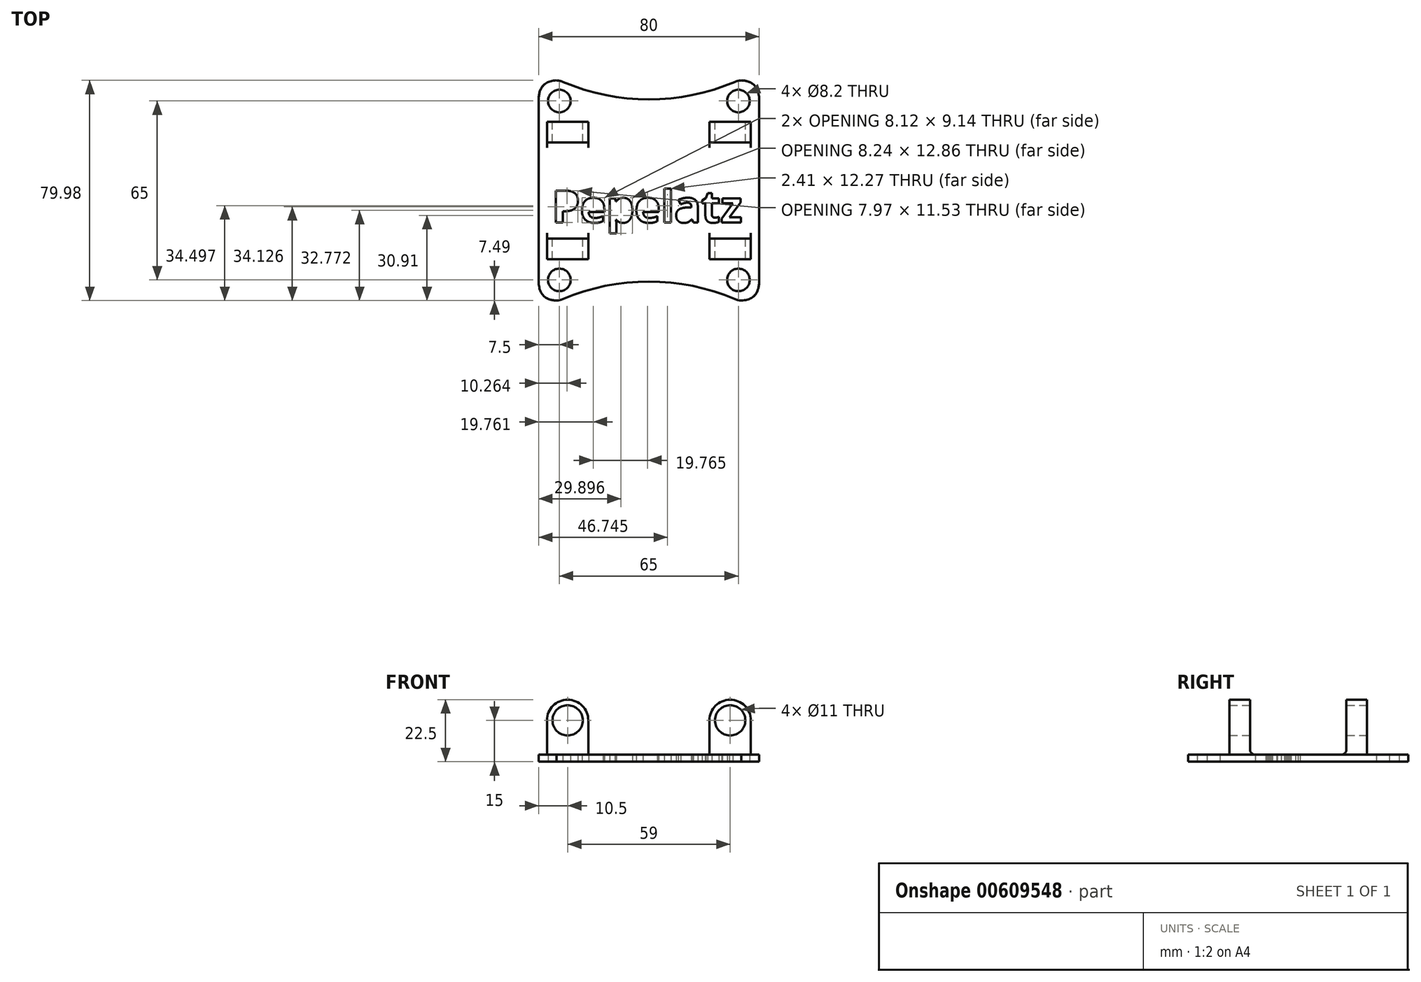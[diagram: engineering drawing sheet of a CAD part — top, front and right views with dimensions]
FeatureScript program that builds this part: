
annotation { "Feature Type Name" : "Feature", "Feature Type Description" : "" }
export const myFeature = defineFeature(function(context is Context, id is Id, definition is map)
    precondition{}
    {
        {
            var Q0;
            Q0=qCreatedBy(makeId("Top.planeOp"),FACE);
            var sketch = newSketch(context, id + "F0", { "sketchPlane" : qUnion([Q0])});
            skLineSegment(sketch, "E0.bottom", {"start": v(-40, 40) * mm, "end": v(-32.5, 40) * mm});
            skLineSegment(sketch, "E0.top", {"start": v(-40, -40) * mm, "end": v(-32.5, -40) * mm});
            skLineSegment(sketch, "E0.left", {"start": v(-40, 40) * mm, "end": v(-40, -40) * mm});
            skLineSegment(sketch, "E0.right", {"start": v(40, 40) * mm, "end": v(40, -40) * mm});
            skPoint(sketch, "E0.middle", {"position": v(0, 0) * mm});
            skLineSegment(sketch, "E1.bottom", {"start": v(-32.5, 32.5) * mm, "end": v(32.5, 32.5) * mm, "construction": true});
            skLineSegment(sketch, "E1.top", {"start": v(-32.5, -32.5) * mm, "end": v(32.5, -32.5) * mm, "construction": true});
            skLineSegment(sketch, "E1.left", {"start": v(-32.5, 32.5) * mm, "end": v(-32.5, -32.5) * mm, "construction": true});
            skLineSegment(sketch, "E1.right", {"start": v(32.5, 32.5) * mm, "end": v(32.5, -32.5) * mm, "construction": true});
            skCircle(sketch, "E2", {"center": v(-32.5, 32.5) * mm, "radius": 4.1 * mm});
            skCircle(sketch, "E3", {"center": v(32.5, 32.5) * mm, "radius": 4.1 * mm});
            skCircle(sketch, "E4", {"center": v(-32.5, -32.5) * mm, "radius": 4.1 * mm});
            skCircle(sketch, "E5", {"center": v(32.5, -32.5) * mm, "radius": 4.1 * mm});
            skLineSegment(sketch, "E6.trimOffspring", {"start": v(32.5, -40) * mm, "end": v(40, -40) * mm});
            skArc(sketch, "E7", {"start": v(32.5, -40) * mm, "mid": v(0, -33.1) * mm, "end": v(-32.5, -40) * mm});
            skPoint(sketch, "E8", {"position": v(-32.5, 40) * mm});
            skPoint(sketch, "E9", {"position": v(32.5, 40) * mm});
            skLineSegment(sketch, "E10.trimOffspring", {"start": v(32.5, 40) * mm, "end": v(40, 40) * mm});
            skArc(sketch, "E11", {"start": v(-32.5, 40) * mm, "mid": v(0, 33.1) * mm, "end": v(32.5, 40) * mm});
            skText(sketch, "E12", { "text": "Pepelatz", "fontName": "OpenSans-Bold.ttf"});
            const initialGuessF0  = {"E12": [-0.03517, -0.01163, 1, 0, 0.01163]};
            skSetInitialGuess(sketch, initialGuessF0);
            skSolve(sketch);
        }
        {
            var Q0;
            Q0 = qSketchRegion(id + "F0", true);
            extrude(context, id + "F1", {"entities" : qUnion([Q0]), "depth" : 2.5 * mm, "offsetDistance" : 25 * mm});
        }
        {
            var Q0;
            Q0=makeQuery(id+"F1.opExtrude","SWEPT_EDGE",EDGE,{"disambiguationData":[OSD([sQuery(id+"F0.wireOp",EDGE,"E0.bottom"),sQuery(id+"F0.wireOp",EDGE,"E0.right")])]});
            var Q1;
            Q1=makeQuery(id+"F1.opExtrude","SWEPT_EDGE",EDGE,{"disambiguationData":[OSD([sQuery(id+"F0.wireOp",EDGE,"E0.top"),sQuery(id+"F0.wireOp",EDGE,"E0.left")])]});
            var Q2;
            Q2=makeQuery(id+"F1.opExtrude","SWEPT_EDGE",EDGE,{"disambiguationData":[OSD([sQuery(id+"F0.wireOp",EDGE,"E0.right"),sQuery(id+"F0.wireOp",EDGE,"E6.trimOffspring")])]});
            var Q3;
            Q3=makeQuery(id+"F1.opExtrude","SWEPT_EDGE",EDGE,{"disambiguationData":[OSD([sQuery(id+"F0.wireOp",EDGE,"E0.bottom"),sQuery(id+"F0.wireOp",EDGE,"E0.left")])]});
            var Q4;
            Q4=makeQuery(id+"F1.opExtrude","SWEPT_EDGE",EDGE,{"disambiguationData":[OSD([sQuery(id+"F0.wireOp",EDGE,"E0.top"),sQuery(id+"F0.wireOp",EDGE,"E7")])]});
            var Q5;
            Q5=makeQuery(id+"F1.opExtrude","SWEPT_EDGE",EDGE,{"disambiguationData":[OSD([sQuery(id+"F0.wireOp",EDGE,"E6.trimOffspring"),sQuery(id+"F0.wireOp",EDGE,"E7")])]});
            var Q6;
            Q6=makeQuery(id+"F1.opExtrude","SWEPT_EDGE",EDGE,{"disambiguationData":[OSD([sQuery(id+"F0.wireOp",EDGE,"E10.trimOffspring"),sQuery(id+"F0.wireOp",EDGE,"E11")])]});
            fillet(context, id + "F2", {"entities" : qUnion([Q0, Q1, Q2, Q3, Q4, Q5, Q6]), "radius" : 7 * mm, "tangentPropagation" : true, "rho" : 0.5, "crossSection" : FilletCrossSection.CONIC, "allowEdgeOverflow" : false});
        }
        {
            var Q0;
            Q0=qCreatedBy(makeId("Front.planeOp"),FACE);
            var sketch = newSketch(context, id + "F3", { "sketchPlane" : qUnion([Q0])});
            skCircle(sketch, "E13", {"center": v(-29.5, 15) * mm, "radius": 5.5 * mm});
            skCircle(sketch, "E14.0", {"center": v(-29.5, 15) * mm, "radius": 7.5 * mm});
            skCircle(sketch, "E15", {"center": v(29.5, 15) * mm, "radius": 7.5 * mm});
            skCircle(sketch, "E16.0", {"center": v(29.5, 15) * mm, "radius": 5.5 * mm});
            skLineSegment(sketch, "E17", {"start": v(-29.5, 15) * mm, "end": v(29.5, 15) * mm, "construction": true});
            skLineSegment(sketch, "E18", {"start": v(0, -3) * mm, "end": v(0, 39.97) * mm, "construction": true});
            skPoint(sketch, "E19", {"position": v(0, 15) * mm});
            skLineSegment(sketch, "E20", {"start": v(-22, 15) * mm, "end": v(-22, 2.5) * mm});
            skLineSegment(sketch, "E21", {"start": v(-22, 2.5) * mm, "end": v(-37, 2.5) * mm});
            skLineSegment(sketch, "E22", {"start": v(-37, 2.5) * mm, "end": v(-37, 15) * mm});
            skLineSegment(sketch, "E23", {"start": v(22, 15) * mm, "end": v(22, 2.5) * mm});
            skLineSegment(sketch, "E24", {"start": v(22, 2.5) * mm, "end": v(37, 2.5) * mm});
            skLineSegment(sketch, "E25", {"start": v(37, 2.5) * mm, "end": v(37, 15) * mm});
            skSolve(sketch);
        }
        {
            var Q0;
            Q0 = qSketchRegion(id + "F3", true);
            extrude(context, id + "F4", {"entities" : qUnion([Q0]), "operationType" : NewBodyOperationType.ADD, "endBound" : BoundingType.SYMMETRIC, "depth" : 50 * mm, "offsetDistance" : 25 * mm});
        }
        {
            var Q0;
            Q0 = qSketchRegion(id + "F3", true);
            extrude(context, id + "F5", {"entities" : qUnion([Q0]), "operationType" : NewBodyOperationType.REMOVE, "endBound" : BoundingType.SYMMETRIC, "oppositeDirection" : true, "depth" : 35 * mm, "offsetDistance" : 25 * mm});
        }
        {
            var Q0;
            {var subQ0=sQuery(id+"F3.wireOp",EDGE,"E22");var subQ1=sQuery(id+"F3.wireOp",EDGE,"E21");var subQ2=sQuery(id+"F3.wireOp",EDGE,"E20");var subQ3=sQuery(id+"F3.wireOp",EDGE,"E14.0");var subQ4=sQuery(id+"F3.wireOp",EDGE,"E13");Q0=makeQuery(id+"F5.boolean.opBoolean","SPLIT",EDGE,{"disambiguationData":[TD([makeQuery(id+"F4.opExtrude","CAP_FACE",FACE,{"disambiguationData":[OSD([subQ4,subQ3,subQ2,subQ1,subQ0])],"isStart":false})])],"derivedFrom":makeQuery(id+"F4.opExtrude","SWEPT_EDGE",EDGE,{"disambiguationData":[OSD([subQ1,subQ0])]})});}
            var Q1;
            {var subQ0=sQuery(id+"F3.wireOp",EDGE,"E22");var subQ1=sQuery(id+"F3.wireOp",EDGE,"E21");var subQ2=sQuery(id+"F3.wireOp",EDGE,"E20");var subQ3=sQuery(id+"F3.wireOp",EDGE,"E14.0");var subQ4=sQuery(id+"F3.wireOp",EDGE,"E13");Q1=makeQuery(id+"F5.boolean.opBoolean","SPLIT",EDGE,{"disambiguationData":[TD([makeQuery(id+"F4.opExtrude","CAP_FACE",FACE,{"disambiguationData":[OSD([subQ4,subQ3,subQ2,subQ1,subQ0])],"isStart":false})])],"derivedFrom":makeQuery(id+"F4.opExtrude","SWEPT_EDGE",EDGE,{"disambiguationData":[OSD([subQ2,subQ1])]})});}
            var Q2;
            {var subQ0=sQuery(id+"F3.wireOp",EDGE,"E23");var subQ1=sQuery(id+"F3.wireOp",EDGE,"E25");var subQ2=sQuery(id+"F3.wireOp",EDGE,"E24");var subQ3=sQuery(id+"F3.wireOp",EDGE,"E16.0");var subQ4=sQuery(id+"F3.wireOp",EDGE,"E15");Q2=makeQuery(id+"F5.boolean.opBoolean","SPLIT",EDGE,{"disambiguationData":[TD([makeQuery(id+"F4.opExtrude","CAP_FACE",FACE,{"disambiguationData":[OSD([subQ4,subQ3,subQ0,subQ2,subQ1])],"isStart":false})])],"derivedFrom":makeQuery(id+"F4.opExtrude","SWEPT_EDGE",EDGE,{"disambiguationData":[OSD([subQ0,subQ2])]})});}
            var Q3;
            {var subQ0=sQuery(id+"F3.wireOp",EDGE,"E25");var subQ1=sQuery(id+"F3.wireOp",EDGE,"E24");var subQ2=sQuery(id+"F3.wireOp",EDGE,"E23");var subQ3=sQuery(id+"F3.wireOp",EDGE,"E16.0");var subQ4=sQuery(id+"F3.wireOp",EDGE,"E15");Q3=makeQuery(id+"F5.boolean.opBoolean","SPLIT",EDGE,{"disambiguationData":[TD([makeQuery(id+"F4.opExtrude","CAP_FACE",FACE,{"disambiguationData":[OSD([subQ4,subQ3,subQ2,subQ1,subQ0])],"isStart":false})])],"derivedFrom":makeQuery(id+"F4.opExtrude","SWEPT_EDGE",EDGE,{"disambiguationData":[OSD([subQ1,subQ0])]})});}
            var Q4;
            {var subQ0=sQuery(id+"F3.wireOp",EDGE,"E25");var subQ1=sQuery(id+"F3.wireOp",EDGE,"E24");var subQ2=sQuery(id+"F3.wireOp",EDGE,"E23");var subQ3=sQuery(id+"F3.wireOp",EDGE,"E16.0");var subQ4=sQuery(id+"F3.wireOp",EDGE,"E15");Q4=makeQuery(id+"F5.boolean.opBoolean","SPLIT",EDGE,{"disambiguationData":[TD([makeQuery(id+"F4.opExtrude","CAP_FACE",FACE,{"disambiguationData":[OSD([subQ4,subQ3,subQ2,subQ1,subQ0])],"isStart":true})])],"derivedFrom":makeQuery(id+"F4.opExtrude","SWEPT_EDGE",EDGE,{"disambiguationData":[OSD([subQ1,subQ0])]})});}
            var Q5;
            {var subQ0=sQuery(id+"F3.wireOp",EDGE,"E25");var subQ1=sQuery(id+"F3.wireOp",EDGE,"E24");var subQ2=sQuery(id+"F3.wireOp",EDGE,"E23");var subQ3=sQuery(id+"F3.wireOp",EDGE,"E16.0");var subQ4=sQuery(id+"F3.wireOp",EDGE,"E15");Q5=makeQuery(id+"F5.boolean.opBoolean","SPLIT",EDGE,{"disambiguationData":[TD([makeQuery(id+"F4.opExtrude","CAP_FACE",FACE,{"disambiguationData":[OSD([subQ4,subQ3,subQ2,subQ1,subQ0])],"isStart":true})])],"derivedFrom":makeQuery(id+"F4.opExtrude","SWEPT_EDGE",EDGE,{"disambiguationData":[OSD([subQ2,subQ1])]})});}
            var Q6;
            {var subQ0=sQuery(id+"F3.wireOp",EDGE,"E22");var subQ1=sQuery(id+"F3.wireOp",EDGE,"E21");var subQ2=sQuery(id+"F3.wireOp",EDGE,"E20");var subQ3=sQuery(id+"F3.wireOp",EDGE,"E14.0");var subQ4=sQuery(id+"F3.wireOp",EDGE,"E13");Q6=makeQuery(id+"F5.boolean.opBoolean","SPLIT",EDGE,{"disambiguationData":[TD([makeQuery(id+"F4.opExtrude","CAP_FACE",FACE,{"disambiguationData":[OSD([subQ4,subQ3,subQ2,subQ1,subQ0])],"isStart":true})])],"derivedFrom":makeQuery(id+"F4.opExtrude","SWEPT_EDGE",EDGE,{"disambiguationData":[OSD([subQ2,subQ1])]})});}
            var Q7;
            {var subQ0=sQuery(id+"F3.wireOp",EDGE,"E22");var subQ1=sQuery(id+"F3.wireOp",EDGE,"E21");var subQ2=sQuery(id+"F3.wireOp",EDGE,"E20");var subQ3=sQuery(id+"F3.wireOp",EDGE,"E14.0");var subQ4=sQuery(id+"F3.wireOp",EDGE,"E13");Q7=makeQuery(id+"F5.boolean.opBoolean","SPLIT",EDGE,{"disambiguationData":[TD([makeQuery(id+"F4.opExtrude","CAP_FACE",FACE,{"disambiguationData":[OSD([subQ4,subQ3,subQ2,subQ1,subQ0])],"isStart":true})])],"derivedFrom":makeQuery(id+"F4.opExtrude","SWEPT_EDGE",EDGE,{"disambiguationData":[OSD([subQ1,subQ0])]})});}
            var Q8;
            Q8=makeQuery(id+"F5.boolean.opBoolean","COPY",EDGE,{"derivedFrom":makeQuery(id+"F5.opExtrude","CAP_EDGE",EDGE,{"disambiguationData":[OSD([sQuery(id+"F3.wireOp",EDGE,"E21")])],"isStart":false})});
            var Q9;
            Q9=makeQuery(id+"F4.opExtrude","CAP_EDGE",EDGE,{"disambiguationData":[OSD([sQuery(id+"F3.wireOp",EDGE,"E21")])],"isStart":false});
            var Q10;
            Q10=makeQuery(id+"F5.boolean.opBoolean","COPY",EDGE,{"derivedFrom":makeQuery(id+"F5.opExtrude","CAP_EDGE",EDGE,{"disambiguationData":[OSD([sQuery(id+"F3.wireOp",EDGE,"E21")])],"isStart":true})});
            var Q11;
            Q11=makeQuery(id+"F4.opExtrude","CAP_EDGE",EDGE,{"disambiguationData":[OSD([sQuery(id+"F3.wireOp",EDGE,"E21")])],"isStart":true});
            var Q12;
            Q12=makeQuery(id+"F4.opExtrude","CAP_EDGE",EDGE,{"disambiguationData":[OSD([sQuery(id+"F3.wireOp",EDGE,"E24")])],"isStart":true});
            var Q13;
            Q13=makeQuery(id+"F5.boolean.opBoolean","COPY",EDGE,{"derivedFrom":makeQuery(id+"F5.opExtrude","CAP_EDGE",EDGE,{"disambiguationData":[OSD([sQuery(id+"F3.wireOp",EDGE,"E24")])],"isStart":false})});
            var Q14;
            Q14=makeQuery(id+"F4.opExtrude","CAP_EDGE",EDGE,{"disambiguationData":[OSD([sQuery(id+"F3.wireOp",EDGE,"E24")])],"isStart":false});
            var Q15;
            Q15=makeQuery(id+"F5.boolean.opBoolean","COPY",EDGE,{"derivedFrom":makeQuery(id+"F5.opExtrude","CAP_EDGE",EDGE,{"disambiguationData":[OSD([sQuery(id+"F3.wireOp",EDGE,"E24")])],"isStart":true})});
            fillet(context, id + "F6", {"entities" : qUnion([Q0, Q1, Q2, Q3, Q4, Q5, Q6, Q7, Q8, Q9, Q10, Q11, Q12, Q13, Q14, Q15]), "radius" : 2 * mm, "tangentPropagation" : true, "allowEdgeOverflow" : false});
        }
    });
